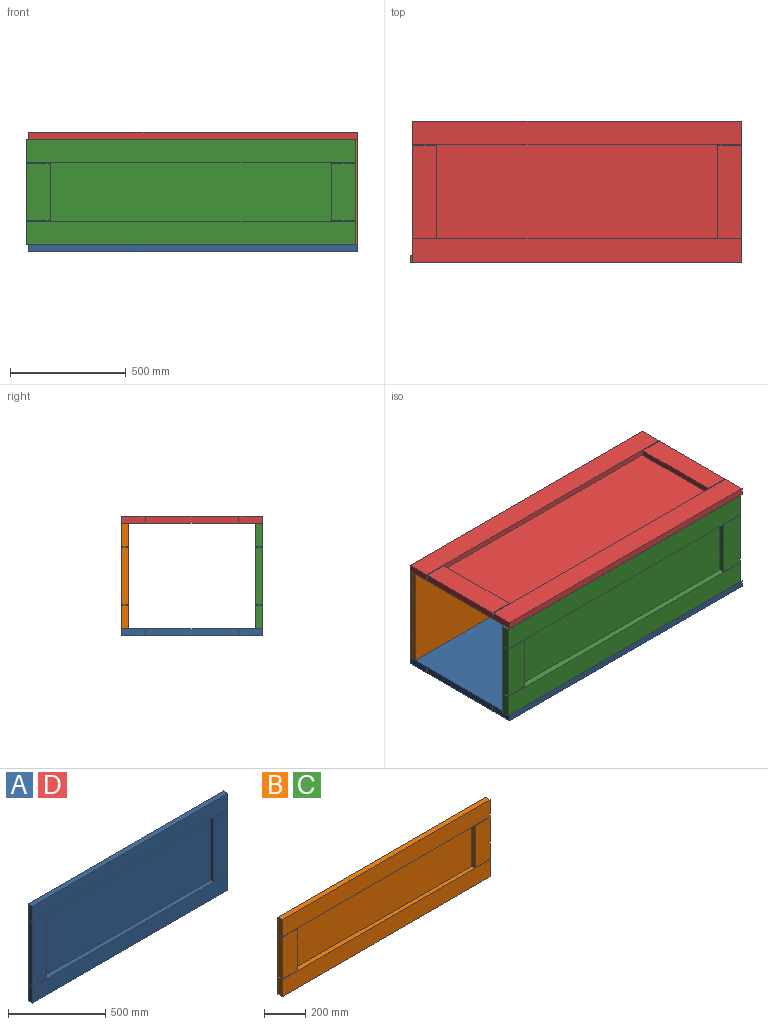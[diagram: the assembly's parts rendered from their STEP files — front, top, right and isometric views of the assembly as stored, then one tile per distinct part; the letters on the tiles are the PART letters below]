
ASSEMBLY  parts=4 mates=9
PART A: 18 faces, bbox 1422.4x31x609.6 mm
  f0: plane 1422.4x406.4mm, normal (0,-1,0), area 496515.1mm2, adj f1,f3,f6,f8,f10,f11,f12,f14
  f1: plane 609.6x30.96mm, normal (1,0,0), area 18741.9mm2, adj f0,f2,f4,f5,f6,f7,f8,f9
  f2: plane 1422.4x30.96mm, normal (0,0,1), area 44032.2mm2, adj f1,f3,f5,f7
  f3: plane 609.6x30.96mm, normal (-1,0,0), area 18741.9mm2, adj f0,f2,f4,f5,f6,f7,f8,f9
  f4: plane 1422.4x30.96mm, normal (0,0,-1), area 44032.2mm2, adj f1,f3,f5,f9
  f5: plane 1422.4x609.6mm, normal (0,1,0), area 867095mm2, adj f1,f2,f3,f4
  f6: plane 1422.4x25.4mm, normal (0,0,-1), area 36129mm2, adj f0,f1,f3,f7
  f7: plane 1422.4x101.6mm, normal (0,-1,0), area 144515.8mm2, adj f1,f2,f3,f6
  f8: plane 1422.4x25.4mm, normal (0,0,1), area 36129mm2, adj f0,f1,f3,f9
  f9: plane 1422.4x101.6mm, normal (0,-1,0), area 144515.8mm2, adj f1,f3,f4,f8
  f10: plane 101.6x25.4mm, normal (0,0,1), area 2580.6mm2, adj f0,f3,f12,f13
  f11: plane 101.6x25.4mm, normal (0,0,-1), area 2580.6mm2, adj f0,f3,f12,f13
  f12: plane 401.32x25.4mm, normal (1,0,0), area 10193.5mm2, adj f0,f10,f11,f13
  f13: plane 401.32x101.6mm, normal (0,-1,0), area 40774.1mm2, adj f3,f10,f11,f12
  f14: plane 101.6x25.4mm, normal (0,0,1), area 2580.6mm2, adj f0,f1,f15,f17
  f15: plane 401.32x25.4mm, normal (-1,0,0), area 10193.5mm2, adj f0,f14,f16,f17
  f16: plane 101.6x25.4mm, normal (0,0,-1), area 2580.6mm2, adj f0,f1,f15,f17
  f17: plane 401.32x101.6mm, normal (0,-1,0), area 40774.1mm2, adj f1,f14,f15,f16
PART B: 18 faces, bbox 1422.4x31x457.2 mm
  f0: plane 1422.4x254mm, normal (0,-1,0), area 310709.1mm2, adj f1,f3,f6,f8,f10,f11,f12,f14
  f1: plane 457.2x30.96mm, normal (1,0,0), area 14024.2mm2, adj f0,f2,f4,f5,f6,f7,f8,f9
  f2: plane 1422.4x30.96mm, normal (0,0,1), area 44032.2mm2, adj f1,f3,f5,f7
  f3: plane 457.2x30.96mm, normal (-1,0,0), area 14024.2mm2, adj f0,f2,f4,f5,f6,f7,f8,f9
  f4: plane 1422.4x30.96mm, normal (0,0,-1), area 44032.2mm2, adj f1,f3,f5,f9
  f5: plane 1422.4x457.2mm, normal (0,1,0), area 650321.3mm2, adj f1,f2,f3,f4
  f6: plane 1422.4x25.4mm, normal (0,0,-1), area 36129mm2, adj f0,f1,f3,f7
  f7: plane 1422.4x101.6mm, normal (0,-1,0), area 144515.8mm2, adj f1,f2,f3,f6
  f8: plane 1422.4x25.4mm, normal (0,0,1), area 36129mm2, adj f0,f1,f3,f9
  f9: plane 1422.4x101.6mm, normal (0,-1,0), area 144515.8mm2, adj f1,f3,f4,f8
  f10: plane 101.6x25.4mm, normal (0,0,1), area 2580.6mm2, adj f0,f3,f12,f13
  f11: plane 101.6x25.4mm, normal (0,0,-1), area 2580.6mm2, adj f0,f3,f12,f13
  f12: plane 248.92x25.4mm, normal (1,0,0), area 6322.6mm2, adj f0,f10,f11,f13
  f13: plane 248.92x101.6mm, normal (0,-1,0), area 25290.3mm2, adj f3,f10,f11,f12
  f14: plane 101.6x25.4mm, normal (0,0,1), area 2580.6mm2, adj f0,f1,f15,f17
  f15: plane 248.92x25.4mm, normal (-1,0,0), area 6322.6mm2, adj f0,f14,f16,f17
  f16: plane 101.6x25.4mm, normal (0,0,-1), area 2580.6mm2, adj f0,f1,f15,f17
  f17: plane 248.92x101.6mm, normal (0,-1,0), area 25290.3mm2, adj f1,f14,f15,f16
PART C: same geometry as B
PART D: same geometry as A
PLACE A rot(axis=(1,0,0),90deg) t=(-718.15,-72.46,-432.42)mm
PLACE B rot(axis=(1,0,0),180deg) t=(-718.15,201.39,-203.82)mm fixed
PLACE C t=(-727.68,-346.3,-203.82)mm
PLACE D rot(axis=(-1,0,0),90deg) t=(-718.15,-72.46,24.78)mm
MATE planar D.f3 <-> B.f3  axis (-1,0,0) through (-1429.35,-72.46,40.23)mm
MATE planar D.f5 <-> B.f4  axis (0,0,-1) through (-718.15,-72.46,24.78)mm
MATE planar A.f4 <-> B.f7  axis (0,1,0) through (-718.15,232.34,-447.9)mm
MATE planar C.f7 <-> D.f4  axis (0,-1,0) through (-727.68,-377.26,-26.02)mm
MATE planar A.f5 <-> B.f2  axis (0,0,1) through (-718.15,-72.46,-432.42)mm
MATE parallel B.f5 <-> C.f5  axis (0,-1,0) through (-6.95,201.39,-432.42)mm
MATE planar A.f1 <-> B.f1  axis (1,0,0) through (-6.95,129.47,-437.98)mm
MATE planar D.f5 <-> C.f2  axis (0,0,-1) through (-718.15,-72.46,24.78)mm
MATE planar D.f2 <-> B.f9  axis (0,1,0) through (-718.15,232.34,40.25)mm
